# Revit family: Haworth_BeHold_SmartLocker_EU_PRELIMINARY
name_source: partatom
category: Furniture Systems
units: mm (PartAtom-declared; Revit-internal decimal feet)

## family parameters
Always vertical = Yes
Cut with Voids When Loaded = No
OmniClass Number = 23.40.70.14.64.21
OmniClass Title = Systems Furniture
Part Type = Normal
Room Calculation Point = No
Round Connector Dimension = Use Diameter
Shared = No
Work Plane-Based = No

## types (4) — shared parameters
Actual Depth = 50 cm
Actual Height = 200 cm
Actual Width = 50 cm
Assembly Code = E2020200
Base Height = 16 cm
Depth = 50 cm
Description = Haworth - BeHold - Smart Locker
Door Width = 50 cm
Glide Finish = Haworth _ Polymer _ Black
Height = 200 cm
Manufacturer = Haworth
Model = Haworth - BeHold
Panel Thickness = 2 cm
Panel Thickness Half = 1 cm
Revision Number = 1
Size = Verify Final Dim. w/ Haworth
Top Height = 3 cm
URL = https://www.haworth.com
URL - Product = https://www.haworth.com
Warranty = http://www.haworth.com
Width = 50 cm
zero-valued in all types: Door Gap, Door Offset

## per-type parameters (varying)
| type | 2 Cubbies | 3 Cubbies | 4 Cubbies | 5 Cubbies |
| 4 Cubbies | No | No | Yes | No |
| 2 Cubbies | Yes | No | No | No |
| 3 Cubbies | No | Yes | No | No |
| 5 Cubbies | No | No | No | Yes |

## geometry (parser evidence)
native form markers: Sweep x13
no freeform markers — native parametric forms only
